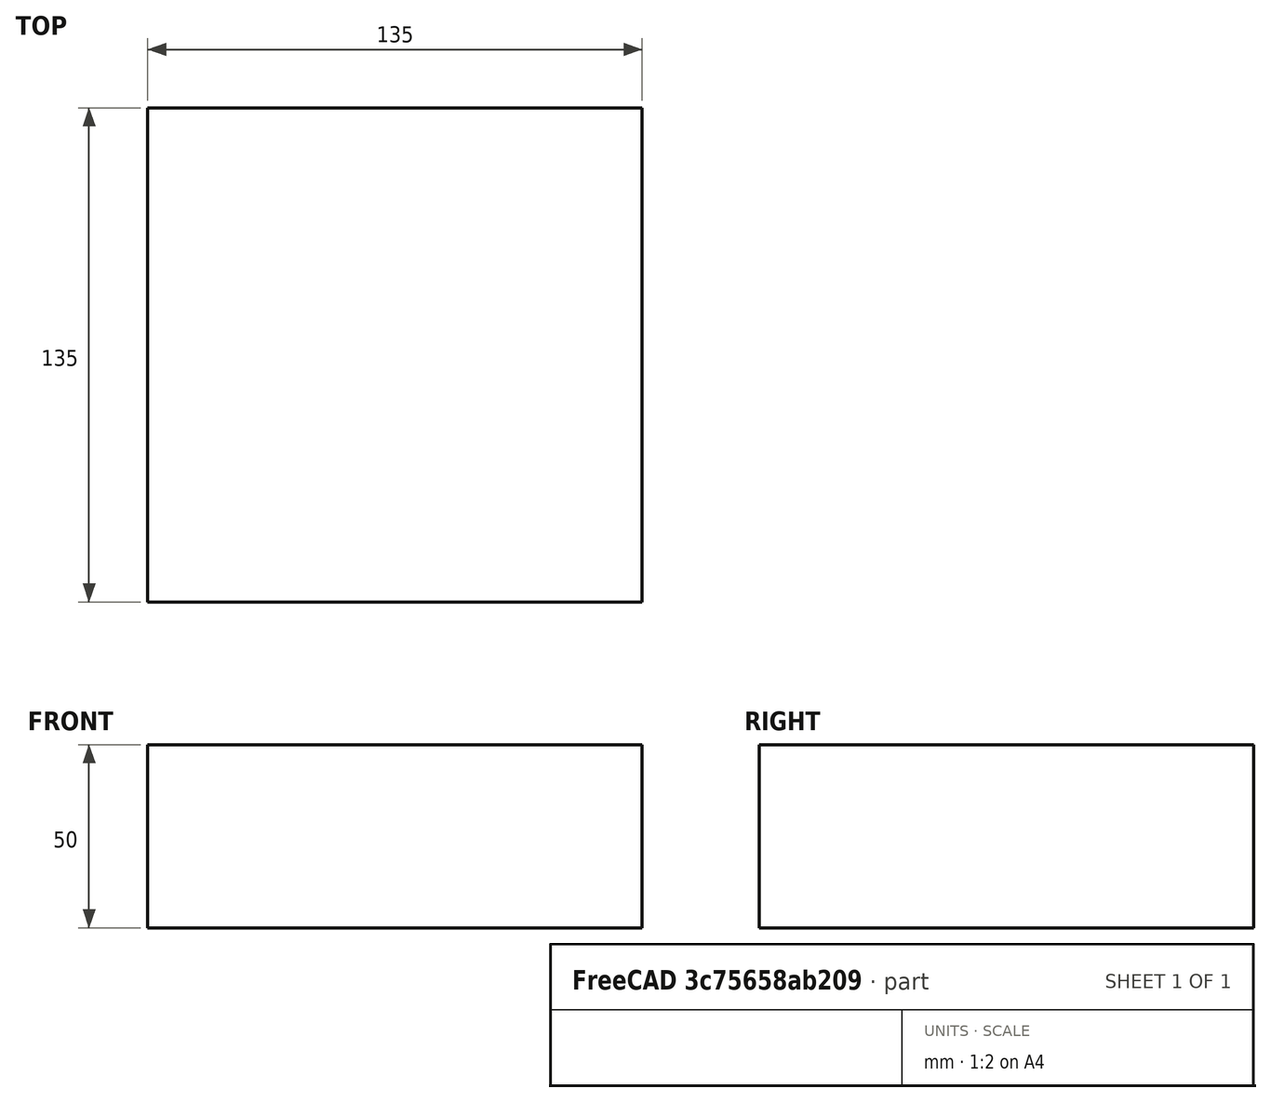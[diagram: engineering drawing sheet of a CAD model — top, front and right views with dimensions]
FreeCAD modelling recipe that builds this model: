
FCSTD DOCUMENT  (FreeCAD 0.15R4671 (Git))
Label: Square Bar 135 EN10059 S235JR
License: All rights reserved
LicenseURL: http://en.wikipedia.org/wiki/All_rights_reserved
objects: Sketcher::SketchObject×1, Part::Extrusion×1
note: 2 computed .brp shape members not serialized (recipe doc carries the construction recipe); baked Part::Feature solids carry a one-line shape summary decoded from their .brp

FEATURE [Sketcher::SketchObject] Sketch
  sketch-geometry (4):
    g0: LineSegment StartX=-67.5 StartY=-67.5 StartZ=0 EndX=67.5 EndY=-67.5 EndZ=0
    g1: LineSegment StartX=67.5 StartY=-67.5 StartZ=0 EndX=67.5 EndY=67.5 EndZ=0
    g2: LineSegment StartX=67.5 StartY=67.5 StartZ=0 EndX=-67.5 EndY=67.5 EndZ=0
    g3: LineSegment StartX=-67.5 StartY=67.5 StartZ=0 EndX=-67.5 EndY=-67.5 EndZ=0
  constraints (12):
    c: Coincident(g0,g1)
    c: Coincident(g1,g2)
    c: Coincident(g2,g3)
    c: Coincident(g3,g0)
    c: Horizontal(g0)
    c: Horizontal(g2)
    c: Vertical(g1)
    c: Vertical(g3)
    c: Symmetric(g1,g0,g-1)
    c: Symmetric(g2,g1,g-2)
    c: Equal(g1,g2)
    c: DistanceY(g1) = 135
FEATURE [Part::Extrusion] Extrude  label="Square Bar 135 EN10059 S235JR"
  Base = -> Sketch
  Dir = (0,0,50)
  Solid = true
